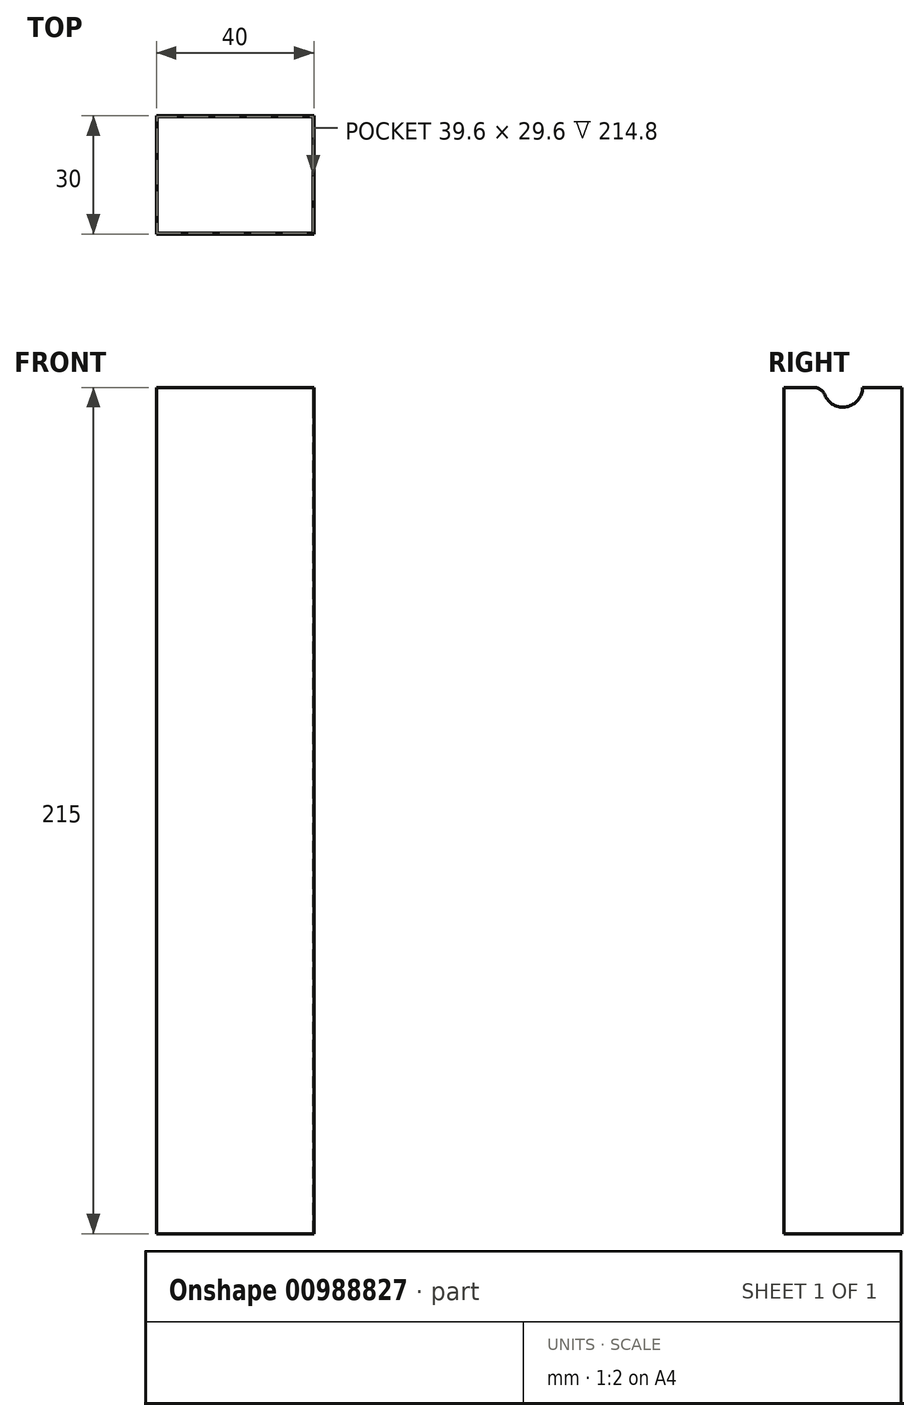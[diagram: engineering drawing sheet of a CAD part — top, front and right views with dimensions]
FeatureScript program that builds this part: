
annotation { "Feature Type Name" : "Feature", "Feature Type Description" : "" }
export const myFeature = defineFeature(function(context is Context, id is Id, definition is map)
    precondition{}
    {
        {
            var Q0;
            Q0=qCreatedBy(makeId("Front.planeOp"),FACE);
            var sketch = newSketch(context, id + "F0", { "sketchPlane" : qUnion([Q0])});
            skLineSegment(sketch, "E0.bottom", {"start": v(-20, 107.5) * mm, "end": v(20, 107.5) * mm});
            skLineSegment(sketch, "E0.top", {"start": v(-20, -107.5) * mm, "end": v(20, -107.5) * mm});
            skLineSegment(sketch, "E0.left", {"start": v(-20, 107.5) * mm, "end": v(-20, -107.5) * mm});
            skLineSegment(sketch, "E0.right", {"start": v(20, 107.5) * mm, "end": v(20, -107.5) * mm});
            skLineSegment(sketch, "E1", {"start": v(-20, 107.5) * mm, "end": v(20, -107.5) * mm, "construction": true});
            skSolve(sketch);
        }
        {
            var Q0;
            Q0=qSketchRegion(id+"F0",true);
            extrude(context, id + "F1", {"entities" : qUnion([Q0]), "endBound" : BoundingType.SYMMETRIC, "depth" : 30 * mm, "offsetDistance" : 25 * mm});
        }
        {
            var Q0;
            Q0=makeQuery(id+"F1.opExtrude","SWEPT_FACE",FACE,{"disambiguationData":[OSD([sQuery(id+"F0.wireOp",EDGE,"E0.bottom")])]});
            var sketch = newSketch(context, id + "F2", { "sketchPlane" : qUnion([Q0])});
            skLineSegment(sketch, "E2.0", {"start": v(-19.8, 14.8) * mm, "end": v(19.8, 14.8) * mm});
            skLineSegment(sketch, "E2.1", {"start": v(-19.8, -14.8) * mm, "end": v(-19.8, 14.8) * mm});
            skLineSegment(sketch, "E2.2", {"start": v(-19.8, -14.8) * mm, "end": v(19.8, -14.8) * mm});
            skLineSegment(sketch, "E2.3", {"start": v(19.8, -14.8) * mm, "end": v(19.8, 14.8) * mm});
            skSolve(sketch);
        }
        {
            var Q0;
            Q0 = qSketchRegion(id + "F2", true);
            extrude(context, id + "F3", {"entities" : qUnion([Q0]), "operationType" : NewBodyOperationType.REMOVE, "oppositeDirection" : true, "depth" : 214.8 * mm, "offsetDistance" : 25 * mm});
        }
        {
            var Q0;
            Q0=makeQuery(id+"F1.opExtrude","SWEPT_FACE",FACE,{"disambiguationData":[OSD([sQuery(id+"F0.wireOp",EDGE,"E0.left")])]});
            var sketch = newSketch(context, id + "F4", { "sketchPlane" : qUnion([Q0])});
            skArc(sketch, "E3", {"start": v(-5, 107.5) * mm, "mid": v(0, 102.5) * mm, "end": v(5, 107.5) * mm});
            skLineSegment(sketch, "E4", {"start": v(-5, 107.5) * mm, "end": v(5, 107.5) * mm});
            skSolve(sketch);
        }
        {
            var Q0;
            Q0 = qSketchRegion(id + "F4", true);
            extrude(context, id + "F5", {"entities" : qUnion([Q0]), "operationType" : NewBodyOperationType.REMOVE, "endBound" : BoundingType.SYMMETRIC, "oppositeDirection" : true, "depth" : 124.8 * mm, "offsetDistance" : 25 * mm});
        }
        {
            var Q0;
            {var subQ0=sQuery(id+"F4.wireOp",EDGE,"E4");var subQ1=sQuery(id+"F4.wireOp",EDGE,"E3");var subQ2=sQuery(id+"F0.wireOp",EDGE,"E0.left");var subQ3=sQuery(id+"F0.wireOp",EDGE,"E0.bottom");Q0=makeQuery(id+"F5.boolean.opBoolean","COPY",EDGE,{"derivedFrom":makeQuery(id+"F5.opExtrude","SWEPT_EDGE",EDGE,{"disambiguationData":[OSD([subQ3,subQ2,subQ1,subQ0]),TDD([makeQuery(id+"F4.imprint","INTERSECT",VERTEX,{"disambiguationData":[OD(0.0)],"derivedFrom":[makeQuery(id+"F1.opExtrude","SWEPT_EDGE",EDGE,{"disambiguationData":[OSD([subQ3,subQ2])]}),subQ1,subQ0]})])]})});}
            var Q1;
            {var subQ0=sQuery(id+"F4.wireOp",EDGE,"E4");var subQ1=sQuery(id+"F4.wireOp",EDGE,"E3");var subQ2=sQuery(id+"F0.wireOp",EDGE,"E0.left");var subQ3=sQuery(id+"F0.wireOp",EDGE,"E0.bottom");Q1=makeQuery(id+"F5.boolean.opBoolean","COPY",EDGE,{"derivedFrom":makeQuery(id+"F5.opExtrude","SWEPT_EDGE",EDGE,{"disambiguationData":[OSD([subQ3,subQ2,subQ1,subQ0]),TDD([makeQuery(id+"F4.imprint","INTERSECT",VERTEX,{"disambiguationData":[OD(1.0)],"derivedFrom":[makeQuery(id+"F1.opExtrude","SWEPT_EDGE",EDGE,{"disambiguationData":[OSD([subQ3,subQ2])]}),subQ1,subQ0]})])]})});}
            fillet(context, id + "F6", {"entities" : qUnion([Q0, Q1]), "radius" : 3 * mm, "tangentPropagation" : true, "allowEdgeOverflow" : false});
        }
    });
